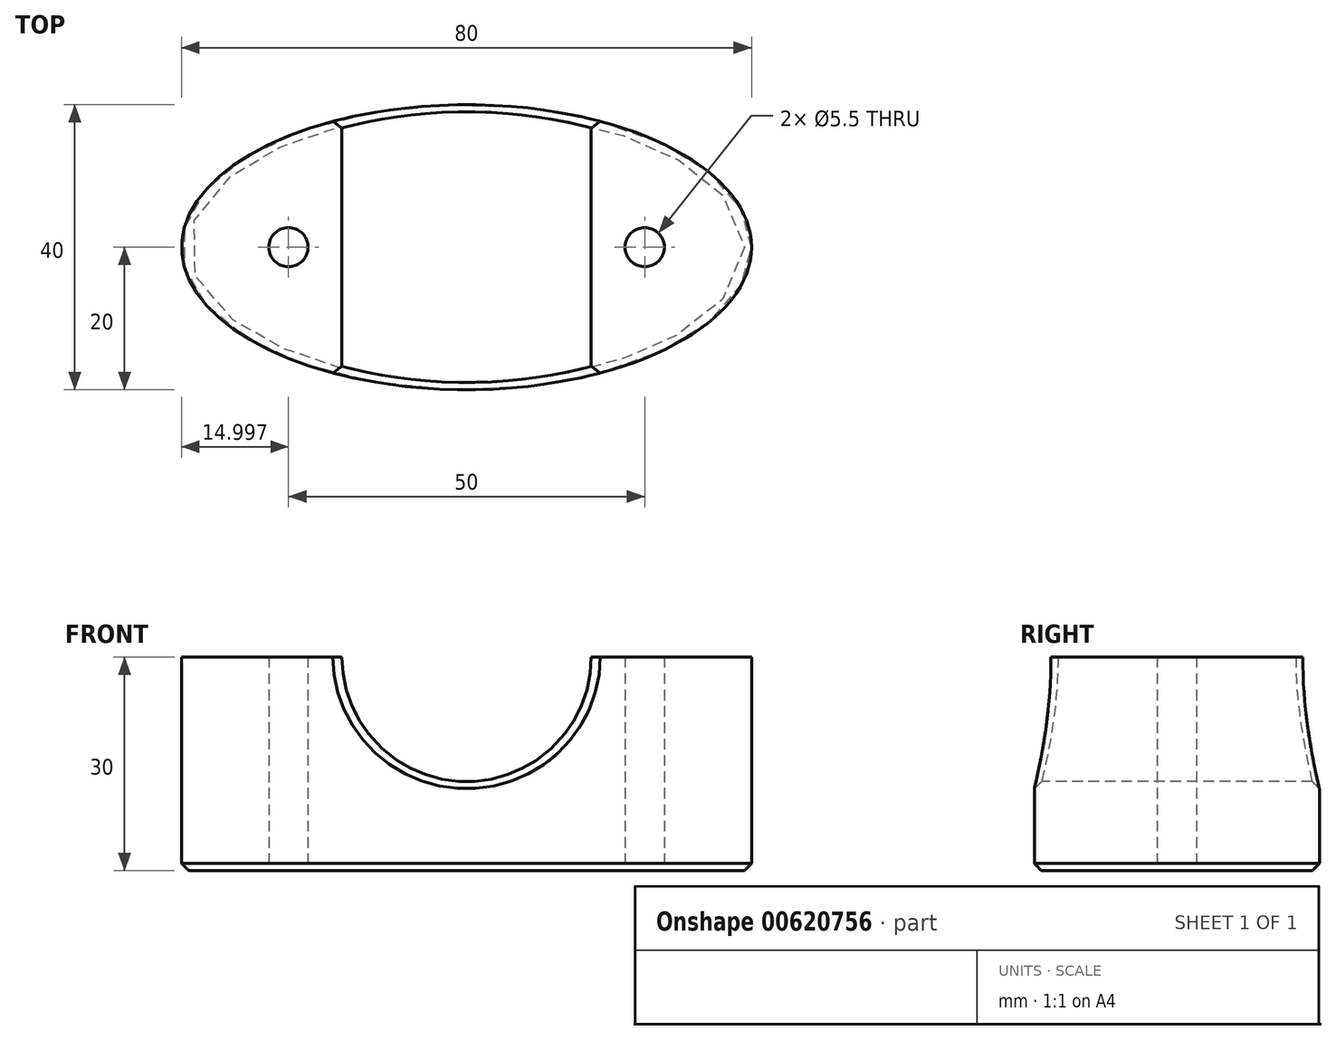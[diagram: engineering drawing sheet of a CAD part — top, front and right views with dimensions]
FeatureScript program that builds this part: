
annotation { "Feature Type Name" : "Feature", "Feature Type Description" : "" }
export const myFeature = defineFeature(function(context is Context, id is Id, definition is map)
    precondition{}
    {
        {
            var Q0;
            Q0=qCreatedBy(makeId("Top.planeOp"),FACE);
            var sketch = newSketch(context, id + "F0", { "sketchPlane" : qUnion([Q0])});
            skEllipse(sketch, "E0", {"center": v(-491.46, 0) * mm, "majorRadius": 40 * mm, "minorRadius": 20 * mm, "majorAxis": v(1, 0)});
            skSolve(sketch);
        }
        {
            var Q0;
            Q0=makeQuery(id+"F0.imprint","IMPRINT",FACE,{"disambiguationData":[TD([[makeQuery(id+"F0.imprint","IMPRINT",EDGE,{"derivedFrom":sQuery(id+"F0.wireOp",EDGE,"E0")}),1.0]])]});
            extrude(context, id + "F1", {"entities" : qUnion([Q0]), "depth" : 30 * mm, "offsetDistance" : 25 * mm});
        }
        {
            var Q0;
            Q0=makeQuery(id+"F1.opExtrude","CAP_FACE",FACE,{"disambiguationData":[OSD([sQuery(id+"F0.wireOp",EDGE,"E0")])],"isStart":true});
            var sketch = newSketch(context, id + "F2", { "sketchPlane" : qUnion([Q0])});
            skLineSegment(sketch, "E1", {"start": v(-491.46, 0) * mm, "end": v(-516.46, 0) * mm});
            skLineSegment(sketch, "E2", {"start": v(-491.46, 0) * mm, "end": v(-466.46, 0) * mm});
            skSolve(sketch);
        }
        {
            var Q0;
            Q0=sQuery(id+"F2.wireOp",VERTEX,"E1.end");
            var Q1;
            Q1=sQuery(id+"F2.wireOp",VERTEX,"E2.end");
            var Q2;
            Q2=makeQuery(id+"F1.opExtrude","SWEPT_BODY",BODY,{"disambiguationData":[OSD([sQuery(id+"F0.wireOp",EDGE,"E0")])]});
            hole(context, id + "F3", {"style" : HoleStyle.SIMPLE, "endStyle" : HoleEndStyle.THROUGH, "standardTappedOrClearance" : lookupTablePath({ "standard" : "ISO", "fit" : "Normal", "size" : "M5", "type" : "Clearance" }), "standardBlindInLast" : lookupTablePath({ "fit" : "Standard", "standard" : "ISO", "size" : "M5", "type" : "Clearance" }), "holeDiameter" : 5.5 * mm, "majorDiameter" : 5 * mm, "isTappedThrough" : true, "tappedDepth" : 12 * mm, "tapClearance" : 3, "locations" : qUnion([Q0, Q1]), "scope" : qUnion([Q2])});
        }
        {
            var Q0;
            Q0=qCreatedBy(makeId("Front.planeOp"),FACE);
            var sketch = newSketch(context, id + "F4", { "sketchPlane" : qUnion([Q0])});
            skCircle(sketch, "E3", {"center": v(-491.46, 30) * mm, "radius": 17.5 * mm});
            skLineSegment(sketch, "E4", {"start": v(-469.21, 30) * mm, "end": v(-513.71, 30) * mm});
            skLineSegment(sketch, "E5", {"start": v(-519.21, 30) * mm, "end": v(-531.46, 30) * mm});
            skLineSegment(sketch, "E6", {"start": v(-451.46, 30) * mm, "end": v(-463.71, 30) * mm});
            skSolve(sketch);
        }
        {
            var Q0;
            {var subQ0=sQuery(id+"F4.wireOp",EDGE,"E4");var subQ1=sQuery(id+"F4.wireOp",EDGE,"E3");var subQ2=makeQuery(id+"F4.imprint","INTERSECT",VERTEX,{"disambiguationData":[OD(0.0)],"derivedFrom":[subQ1,subQ0]});Q0=makeQuery(id+"F4.imprint","IMPRINT",FACE,{"disambiguationData":[TD([[makeQuery(id+"F4.imprint","IMPRINT",EDGE,{"disambiguationData":[TD([[subQ2,-1.0]])],"derivedFrom":subQ1}),1.0]])]});}
            var Q1;
            Q1=sQuery(id+"F4.wireOp",EDGE,"E3");
            extrude(context, id + "F5", {"entities" : qUnion([Q0]), "operationType" : NewBodyOperationType.REMOVE, "surfaceEntities" : qUnion([Q1]), "oppositeDirection" : true, "depth" : 25 * mm, "offsetDistance" : 25 * mm});
        }
        {
            var Q0;
            Q0=makeQuery(id+"F5.boolean.opBoolean","COPY",FACE,{"derivedFrom":makeQuery(id+"F5.opExtrude","CAP_FACE",FACE,{"disambiguationData":[OSD([sQuery(id+"F4.wireOp",EDGE,"E3"),sQuery(id+"F4.wireOp",EDGE,"E4")])],"isStart":true})});
            extrude(context, id + "F6", {"entities" : qUnion([Q0]), "operationType" : NewBodyOperationType.REMOVE, "oppositeDirection" : true, "depth" : 25 * mm, "offsetDistance" : 25 * mm});
        }
        {
            var Q0;
            Q0=makeQuery(id+"F6.boolean.opBoolean","INTERSECT",EDGE,{"derivedFrom":[makeQuery(id+"F1.opExtrude","SWEPT_FACE",FACE,{"disambiguationData":[OSD([sQuery(id+"F0.wireOp",EDGE,"E0")])]}),makeQuery(id+"F6.opExtrude","SWEPT_FACE",FACE,{"disambiguationData":[OSD([sQuery(id+"F4.wireOp",EDGE,"E3")])]})]});
            var Q1;
            Q1=makeQuery(id+"F5.boolean.opBoolean","INTERSECT",EDGE,{"derivedFrom":[makeQuery(id+"F1.opExtrude","SWEPT_FACE",FACE,{"disambiguationData":[OSD([sQuery(id+"F0.wireOp",EDGE,"E0")])]}),makeQuery(id+"F5.opExtrude","SWEPT_FACE",FACE,{"disambiguationData":[OSD([sQuery(id+"F4.wireOp",EDGE,"E3")])]})]});
            var Q2;
            Q2=makeQuery(id+"F1.opExtrude","CAP_EDGE",EDGE,{"disambiguationData":[OSD([sQuery(id+"F0.wireOp",EDGE,"E0")])],"isStart":true});
            chamfer(context, id + "F7", {"entities" : qUnion([Q0, Q1, Q2]), "width" : 1 * mm, "tangentPropagation" : true});
        }
    });
